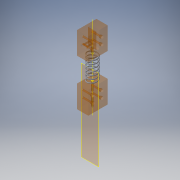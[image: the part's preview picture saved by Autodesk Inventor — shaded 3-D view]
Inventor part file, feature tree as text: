
AUTODESK INVENTOR PART (.ipt)
format: ipt  version: 2016 (Build 200138000, 138)  size: 483,328 bytes
history: native  units: in
note: dims shown in document units (in); Inventor stores cm internally (conversion verified against a paired STEP export)
features: other x5, surface_op x2, plane x1, helix x1, sketch x1
ambient origin geometry x8: Origin, YZ Plane, XZ Plane, XY Plane, X Axis, Y Axis, Z Axis, Center Point
bodies: Solid1 (feature_tree)
feature tree (10):
  other  "Work Axis1"
  other  "Work Point1"
  other  "Work Point2"
  plane  "Work Plane1"
  helix  "Coil1"  [1 undecoded]
  sketch  "Sketch1"  dims[d1=0.429in d2=2.2732in d3=1.0in d4=2.1932in d5=2.7559in d6=0.0in d7=90.0deg d8=90.0deg d9=0.0in d10=0.0in]
  surface_op  "Surface1"
  surface_op  "Surface2"
  other  "Srf1"
  other  "Srf2"
note: 1 required parameter value undecoded (feature->parameter linkage not recoverable at this tier; creation-order binding heuristic only, values carry confidence <= 0.55)
